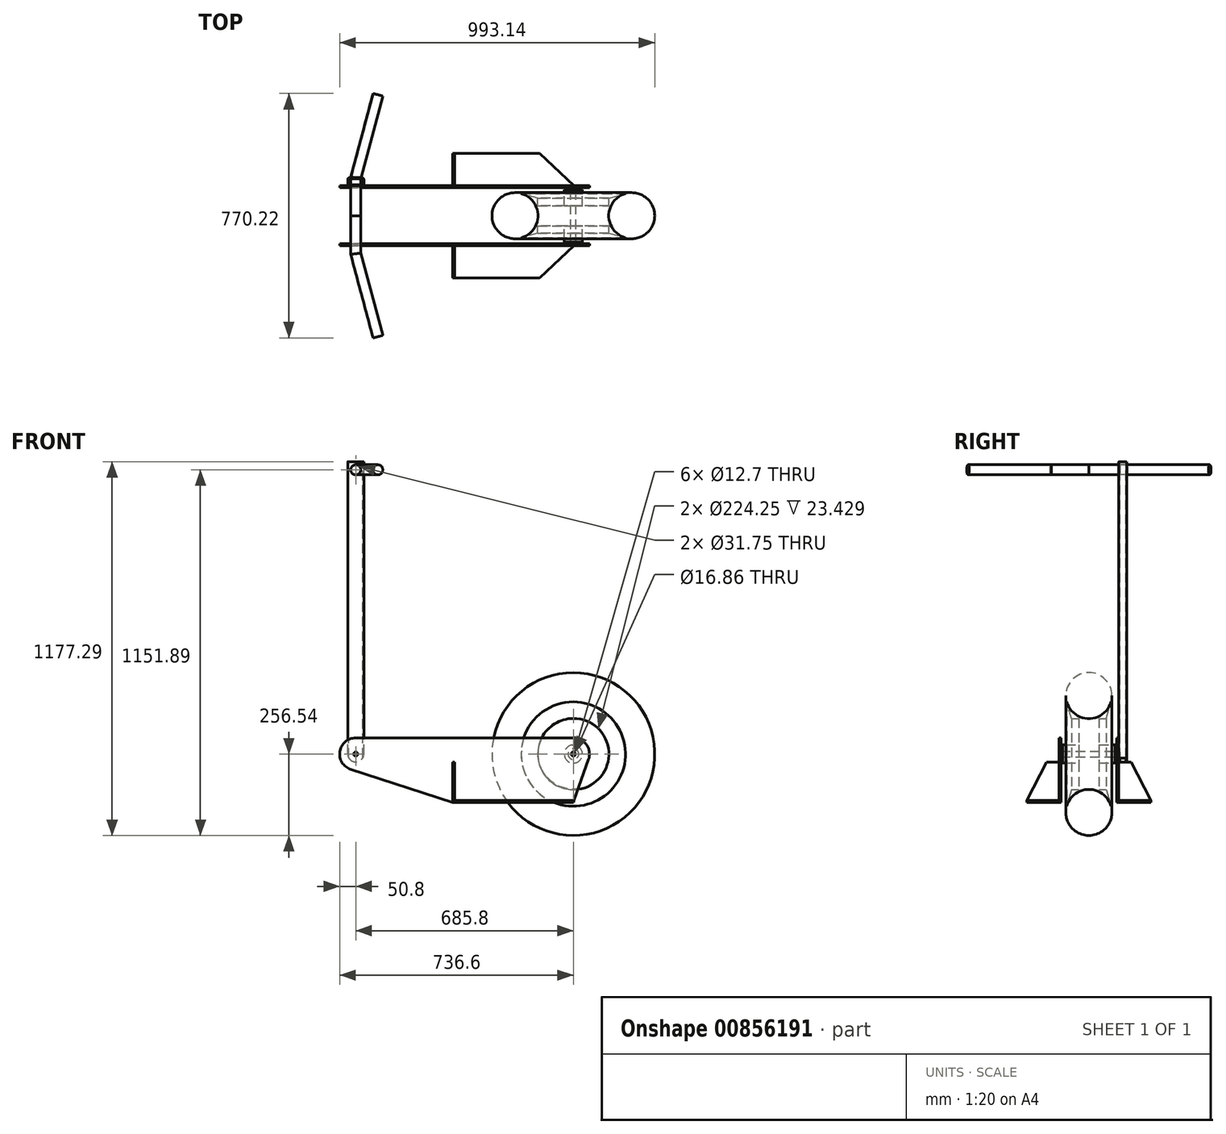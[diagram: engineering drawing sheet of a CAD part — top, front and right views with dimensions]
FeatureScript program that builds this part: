
annotation { "Feature Type Name" : "Feature", "Feature Type Description" : "" }
export const myFeature = defineFeature(function(context is Context, id is Id, definition is map)
    precondition{}
    {
        {
            var Q0;
            Q0=qCreatedBy(makeId("Front.planeOp"),FACE);
            var sketch = newSketch(context, id + "F0", { "sketchPlane" : qUnion([Q0])});
            skCircle(sketch, "E0", {"center": v(0, 0) * mm, "radius": 256.54 * mm});
            skPoint(sketch, "E0.first.point", {"position": v(0, 256.54) * mm});
            skPoint(sketch, "E0.second.point", {"position": v(248.73, -62.84) * mm});
            skPoint(sketch, "E0.third.point", {"position": v(-198.26, -162.81) * mm});
            skCircle(sketch, "E1", {"center": v(0, 0) * mm, "radius": 152.4 * mm});
            skPoint(sketch, "E1.first.point", {"position": v(0, 152.4) * mm});
            skPoint(sketch, "E1.second.point", {"position": v(151.83, -13.14) * mm});
            skPoint(sketch, "E1.third.point", {"position": v(-136.4, -68) * mm});
            skSolve(sketch);
        }
        {
            var Q0;
            Q0=qCreatedBy(makeId("Right.planeOp"),FACE);
            var sketch = newSketch(context, id + "F1", { "sketchPlane" : qUnion([Q0])});
            skPoint(sketch, "E2.0", {"position": v(0, 256.54) * mm});
            skLineSegment(sketch, "E2.1", {"start": v(0, -256.54) * mm, "end": v(0, 256.54) * mm, "construction": true});
            skLineSegment(sketch, "E3.bottom", {"start": v(82.52, 28.57) * mm, "end": v(-82.52, 28.58) * mm});
            skLineSegment(sketch, "E3.top", {"start": v(82.52, -28.57) * mm, "end": v(-82.52, -28.57) * mm});
            skLineSegment(sketch, "E3.left", {"start": v(82.52, 28.57) * mm, "end": v(82.52, 8.43) * mm});
            skLineSegment(sketch, "E3.right", {"start": v(-82.52, 28.58) * mm, "end": v(-82.52, 8.43) * mm});
            skPoint(sketch, "E3.middle", {"position": v(0, 0) * mm});
            skArc(sketch, "E4", {"start": v(71.4, 196.84) * mm, "mid": v(0, 256.54) * mm, "end": v(-71.4, 196.84) * mm});
            skLineSegment(sketch, "E5", {"start": v(71.4, 196.84) * mm, "end": v(-71.4, 196.84) * mm, "construction": true});
            skCircle(sketch, "E6", {"center": v(0, 184) * mm, "radius": 72.54 * mm});
            skLineSegment(sketch, "E7", {"start": v(69.84, 164.42) * mm, "end": v(55.18, 112.13) * mm});
            skLineSegment(sketch, "E8.MirrorCS", {"start": v(-69.84, 164.42) * mm, "end": v(-55.18, 112.13) * mm});
            skLineSegment(sketch, "E9", {"start": v(87.95, 8.43) * mm, "end": v(87.95, 16.86) * mm});
            skPoint(sketch, "E9.startSnap0", {"position": v(82.52, 0) * mm});
            skLineSegment(sketch, "E10", {"start": v(87.95, 16.86) * mm, "end": v(82.52, 16.86) * mm});
            skLineSegment(sketch, "E11", {"start": v(87.95, 0) * mm, "end": v(-87.95, 0) * mm});
            skLineSegment(sketch, "E12.MirrorCS", {"start": v(-87.95, 16.86) * mm, "end": v(-82.52, 16.86) * mm});
            skLineSegment(sketch, "E13.MirrorCS", {"start": v(-87.95, 8.43) * mm, "end": v(-87.95, 16.86) * mm});
            skLineSegment(sketch, "E14", {"start": v(31.75, 28.58) * mm, "end": v(31.75, 112.13) * mm});
            skLineSegment(sketch, "E15", {"start": v(31.75, 112.13) * mm, "end": v(55.18, 112.13) * mm});
            skLineSegment(sketch, "E16", {"start": v(55.18, 112.13) * mm, "end": v(31.75, 112.13) * mm});
            skLineSegment(sketch, "E17", {"start": v(-31.75, 28.58) * mm, "end": v(-31.75, 112.13) * mm});
            skLineSegment(sketch, "E18.trimOffspring", {"start": v(-31.75, 112.13) * mm, "end": v(-55.18, 112.13) * mm});
            skLineSegment(sketch, "E19", {"start": v(-87.95, 8.43) * mm, "end": v(87.95, 8.43) * mm});
            skLineSegment(sketch, "E20.trimOffspring", {"start": v(-82.52, 0) * mm, "end": v(-82.52, -28.57) * mm});
            skLineSegment(sketch, "E21.trimOffspring", {"start": v(82.52, 0) * mm, "end": v(82.52, -28.58) * mm});
            skSolve(sketch);
        }
        {
            var Q0;
            {var subQ0=sQuery(id+"F1.wireOp",EDGE,"E7");Q0=makeQuery(id+"F1.imprint","IMPRINT",FACE,{"disambiguationData":[TD([[makeQuery(id+"F1.imprint","IMPRINT",EDGE,{"derivedFrom":subQ0}),-1.0]])]});}
            var Q1;
            {var subQ0=sQuery(id+"F1.wireOp",EDGE,"E3.left");var subQ1=sQuery(id+"F1.wireOp",EDGE,"E3.bottom");var subQ2=makeQuery(id+"F1.imprint","INTERSECT",VERTEX,{"derivedFrom":[subQ1,subQ0]});Q1=makeQuery(id+"F1.imprint","IMPRINT",FACE,{"disambiguationData":[TD([[makeQuery(id+"F1.imprint","IMPRINT",EDGE,{"disambiguationData":[TD([[subQ2,-1.0]])],"derivedFrom":subQ1}),1.0]])]});}
            var Q2;
            {var subQ4=sQuery(id+"F1.wireOp",EDGE,"E9");Q2=makeQuery(id+"F1.imprint","IMPRINT",FACE,{"disambiguationData":[TD([[makeQuery(id+"F1.imprint","IMPRINT",EDGE,{"derivedFrom":subQ4}),1.0]])]});}
            var Q3;
            {var subQ0=sQuery(id+"F1.wireOp",EDGE,"E12.MirrorCS");Q3=makeQuery(id+"F1.imprint","IMPRINT",FACE,{"disambiguationData":[TD([[makeQuery(id+"F1.imprint","IMPRINT",EDGE,{"derivedFrom":subQ0}),-1.0]])]});}
            var Q4;
            Q4=sQuery(id+"F1.wireOp",EDGE,"E11");
            revolve(context, id + "F2", {"surfaceOperationType" : NewSurfaceOperationType.NEW, "entities" : qUnion([Q0, Q1, Q2, Q3]), "axis" : qUnion([Q4]), "revolveType" : RevolveType.FULL});
        }
        {
            var Q0;
            {var subQ0=sQuery(id+"F1.wireOp",EDGE,"E6");var subQ1=makeQuery(id+"F1.imprint","INTERSECT",VERTEX,{"derivedFrom":[subQ0,sQuery(id+"F1.wireOp",EDGE,"E7")]});Q0=makeQuery(id+"F1.imprint","IMPRINT",FACE,{"disambiguationData":[TD([[makeQuery(id+"F1.imprint","IMPRINT",EDGE,{"disambiguationData":[TD([[subQ1,-1.0]])],"derivedFrom":subQ0}),1.0]])]});}
            var Q1;
            Q1=sQuery(id+"F1.wireOp",EDGE,"E11");
            revolve(context, id + "F3", {"surfaceOperationType" : NewSurfaceOperationType.NEW, "entities" : qUnion([Q0]), "axis" : qUnion([Q1]), "revolveType" : RevolveType.FULL});
        }
        {
            var Q0;
            Q0=makeQuery(id+"F2.opRevolve","SWEPT_FACE",FACE,{"disambiguationData":[OSD([sQuery(id+"F1.wireOp",EDGE,"E9")])]});
            var sketch = newSketch(context, id + "F4", { "sketchPlane" : qUnion([Q0])});
            skLineSegment(sketch, "E22", {"start": v(0, 0) * mm, "end": v(685.8, 0) * mm, "construction": true});
            skCircle(sketch, "E23", {"center": v(685.8, 0) * mm, "radius": 256.54 * mm, "construction": true});
            skLineSegment(sketch, "E24", {"start": v(0, -152.4) * mm, "end": v(381, -152.4) * mm, "construction": true});
            skCircle(sketch, "E25.0", {"center": v(0, 0) * mm, "radius": 256.54 * mm, "construction": true});
            skLineSegment(sketch, "E26", {"start": v(-256.54, 0) * mm, "end": v(942.34, 0) * mm, "construction": true});
            skPoint(sketch, "E26.endSnap0", {"position": v(342.9, 0) * mm});
            skLineSegment(sketch, "E27", {"start": v(0, 0) * mm, "end": v(0, -63.15) * mm, "construction": true});
            skPoint(sketch, "E28.visualSharp", {"position": v(-50.8, 25.4) * mm});
            skCircle(sketch, "E29", {"center": v(0, 0) * mm, "radius": 6.35 * mm});
            skCircle(sketch, "E30", {"center": v(685.8, 0) * mm, "radius": 6.35 * mm});
            skLineSegment(sketch, "E31", {"start": v(-105.93, -256.54) * mm, "end": v(75.98, -256.54) * mm, "construction": true});
            skCircle(sketch, "E32", {"center": v(0, 0) * mm, "radius": 152.4 * mm});
            skPoint(sketch, "E33.orphan", {"position": v(-38.1, -152.4) * mm});
            skLineSegment(sketch, "E34", {"start": v(-152.4, 0) * mm, "end": v(-146.05, 0) * mm});
            skArc(sketch, "E35", {"start": v(0, 50.8) * mm, "mid": v(-41.48, 29.33) * mm, "end": v(-47.9, -16.93) * mm});
            skArc(sketch, "E36", {"start": v(701.5, -48.32) * mm, "mid": v(735.98, 7.94) * mm, "end": v(685.8, 50.8) * mm});
            skLineSegment(sketch, "E37", {"start": v(-55.72, 5.2) * mm, "end": v(0, -152.4) * mm});
            skLineSegment(sketch, "E38", {"start": v(0, -152.4) * mm, "end": v(381, -152.4) * mm});
            skLineSegment(sketch, "E39", {"start": v(381, -152.4) * mm, "end": v(701.5, -48.32) * mm});
            skLineSegment(sketch, "E40", {"start": v(0, 50.8) * mm, "end": v(685.8, 50.8) * mm});
            skLineSegment(sketch, "E41", {"start": v(-2.25, -146.05) * mm, "end": v(374.65, -146.05) * mm});
            skLineSegment(sketch, "E42", {"start": v(374.65, -146.05) * mm, "end": v(374.65, 50.8) * mm});
            skLineSegment(sketch, "E43", {"start": v(381, -152.4) * mm, "end": v(381, 50.8) * mm});
            skLineSegment(sketch, "E44", {"start": v(374.65, -146.05) * mm, "end": v(381, -146.05) * mm});
            skLineSegment(sketch, "E45", {"start": v(374.65, -25.4) * mm, "end": v(381, -25.4) * mm});
            skSolve(sketch);
        }
        {
            var Q0;
            Q0=makeQuery(id+"F4.imprint","IMPRINT",FACE,{"disambiguationData":[TD([[makeQuery(id+"F4.imprint","IMPRINT",EDGE,{"derivedFrom":sQuery(id+"F4.wireOp",EDGE,"E29")}),-1.0]])]});
            var Q1;
            {var subQ0=sQuery(id+"F1.wireOp",EDGE,"E9");Q1=makeQuery(id+"F4.imprint","IMPRINT",FACE,{"disambiguationData":[TD([[makeQuery(id+"F4.imprint","IMPRINT",EDGE,{"derivedFrom":makeQuery(id+"F2.opRevolve","SWEPT_EDGE",EDGE,{"disambiguationData":[OSD([subQ0,sQuery(id+"F1.wireOp",EDGE,"E19")])]})}),-1.0]])]});}
            var Q2;
            Q2=makeQuery(id+"F4.imprint","IMPRINT",FACE,{"disambiguationData":[TD([[makeQuery(id+"F4.imprint","IMPRINT",EDGE,{"derivedFrom":sQuery(id+"F4.wireOp",EDGE,"E30")}),-1.0]])]});
            var Q3;
            {var subQ0=sQuery(id+"F4.wireOp",EDGE,"E37");var subQ3=sQuery(id+"F4.wireOp",EDGE,"E41");var subQ5=makeQuery(id+"F4.imprint","INTERSECT",VERTEX,{"derivedFrom":[subQ0,subQ3]});Q3=makeQuery(id+"F4.imprint","IMPRINT",FACE,{"disambiguationData":[TD([[makeQuery(id+"F4.imprint","IMPRINT",EDGE,{"disambiguationData":[TD([[subQ5,-1.0]])],"derivedFrom":subQ3}),-1.0]])]});}
            var Q4;
            {var subQ5=sQuery(id+"F4.wireOp",EDGE,"E42");Q4=makeQuery(id+"F4.imprint","IMPRINT",FACE,{"disambiguationData":[TD([[makeQuery(id+"F4.imprint","IMPRINT",EDGE,{"derivedFrom":subQ5}),1.0]])]});}
            var Q5;
            {var subQ0=sQuery(id+"F4.wireOp",EDGE,"E42");Q5=makeQuery(id+"F4.imprint","IMPRINT",FACE,{"disambiguationData":[TD([[makeQuery(id+"F4.imprint","IMPRINT",EDGE,{"derivedFrom":subQ0}),-1.0]])]});}
            var Q6;
            {var subQ4=sQuery(id+"F4.wireOp",EDGE,"E38");Q6=makeQuery(id+"F4.imprint","IMPRINT",FACE,{"disambiguationData":[TD([[makeQuery(id+"F4.imprint","IMPRINT",EDGE,{"derivedFrom":subQ4}),1.0]])]});}
            var Q7;
            {var subQ1=sQuery(id+"F4.wireOp",EDGE,"E35");Q7=makeQuery(id+"F4.imprint","IMPRINT",FACE,{"disambiguationData":[TD([[makeQuery(id+"F4.imprint","IMPRINT",EDGE,{"derivedFrom":subQ1}),1.0]])]});}
            extrude(context, id + "F5", {"entities" : qUnion([Q0, Q1, Q2, Q3, Q4, Q5, Q6, Q7]), "depth" : 6.35 * mm, "offsetDistance" : 25.4 * mm});
        }
        {
            var Q0;
            Q0=makeQuery(id+"F5.opExtrude","CAP_FACE",FACE,{"disambiguationData":[OSD([sQuery(id+"F4.wireOp",EDGE,"E29"),sQuery(id+"F4.wireOp",EDGE,"E30"),sQuery(id+"F4.wireOp",EDGE,"E35"),sQuery(id+"F4.wireOp",EDGE,"E36"),sQuery(id+"F4.wireOp",EDGE,"E37"),sQuery(id+"F4.wireOp",EDGE,"E38"),sQuery(id+"F4.wireOp",EDGE,"E39"),sQuery(id+"F4.wireOp",EDGE,"E40")])],"isStart":false});
            var sketch = newSketch(context, id + "F6", { "sketchPlane" : qUnion([Q0])});
            skLineSegment(sketch, "E46.0", {"start": v(374.65, -146.05) * mm, "end": v(374.65, 50.8) * mm});
            skLineSegment(sketch, "E46.1", {"start": v(381, -152.4) * mm, "end": v(381, 50.8) * mm});
            skLineSegment(sketch, "E46.2", {"start": v(-2.25, -146.05) * mm, "end": v(374.65, -146.05) * mm});
            skLineSegment(sketch, "E46.3", {"start": v(0, -152.4) * mm, "end": v(381, -152.4) * mm});
            skLineSegment(sketch, "E46.4", {"start": v(-55.72, 5.2) * mm, "end": v(0, -152.4) * mm});
            skLineSegment(sketch, "E46.5", {"start": v(0, 50.8) * mm, "end": v(685.8, 50.8) * mm});
            skLineSegment(sketch, "E47.0", {"start": v(374.65, -146.05) * mm, "end": v(381, -146.05) * mm});
            skLineSegment(sketch, "E48.0", {"start": v(374.65, -25.4) * mm, "end": v(381, -25.4) * mm});
            skSolve(sketch);
        }
        {
            var Q0;
            Q0 = qSketchRegion(id + "F6", true);
            extrude(context, id + "F7", {"entities" : qUnion([Q0]), "operationType" : NewBodyOperationType.ADD, "depth" : 101.6 * mm, "offsetDistance" : 25.4 * mm});
        }
        {
            var Q0;
            Q0=makeQuery(id+"F7.opExtrude","SWEPT_FACE",FACE,{"disambiguationData":[OSD([sQuery(id+"F6.wireOp",EDGE,"E46.0")])]});
            var sketch = newSketch(context, id + "F8", { "sketchPlane" : qUnion([Q0])});
            skLineSegment(sketch, "E49", {"start": v(94.3, 50.8) * mm, "end": v(195.9, -146.05) * mm});
            skPoint(sketch, "E50.0", {"position": v(87.95, -25.4) * mm});
            skLineSegment(sketch, "E51", {"start": v(87.95, -25.4) * mm, "end": v(133.63, -25.4) * mm});
            skSolve(sketch);
        }
        {
            var Q0;
            Q0 = qSketchRegion(id + "F8", true);
            var Q1;
            Q1=makeQuery(id+"F8.imprint","IMPRINT",FACE,{"disambiguationData":[TD([[makeQuery(id+"F8.imprint","IMPRINT",EDGE,{"derivedFrom":sQuery(id+"F8.wireOp",EDGE,"E49")}),1.0]])]});
            var Q2;
            {var subQ0=sQuery(id+"F8.wireOp",EDGE,"E49");var subQ4=sQuery(id+"F8.wireOp",EDGE,"E51");var subQ5=makeQuery(id+"F8.imprint","INTERSECT",VERTEX,{"derivedFrom":[subQ0,subQ4]});Q2=makeQuery(id+"F8.imprint","IMPRINT",FACE,{"disambiguationData":[TD([[makeQuery(id+"F8.imprint","IMPRINT",EDGE,{"disambiguationData":[TD([[subQ5,1.0]])],"derivedFrom":subQ4}),1.0]])]});}
            extrude(context, id + "F9", {"entities" : qUnion([Q0, Q1, Q2]), "operationType" : NewBodyOperationType.REMOVE, "oppositeDirection" : true, "depth" : 25.4 * mm, "offsetDistance" : 25.4 * mm});
        }
        {
            var Q0;
            Q0=makeQuery(id+"F7.opExtrude","CAP_EDGE",EDGE,{"disambiguationData":[OSD([sQuery(id+"F6.wireOp",EDGE,"E46.4")])],"isStart":false});
            chamfer(context, id + "F10", {"entities" : qUnion([Q0]), "width" : 101.6 * mm, "tangentPropagation" : true});
        }
        {
            var Q0;
            Q0=makeQuery(id+"F5.opExtrude","SWEPT_BODY",BODY,{"disambiguationData":[OSD([sQuery(id+"F4.wireOp",EDGE,"E29"),sQuery(id+"F4.wireOp",EDGE,"E30"),sQuery(id+"F4.wireOp",EDGE,"E35"),sQuery(id+"F4.wireOp",EDGE,"E36"),sQuery(id+"F4.wireOp",EDGE,"E37"),sQuery(id+"F4.wireOp",EDGE,"E38"),sQuery(id+"F4.wireOp",EDGE,"E39"),sQuery(id+"F4.wireOp",EDGE,"E40")])]});
            var Q1;
            Q1=qCreatedBy(makeId("Front.planeOp"),FACE);
            mirror(context, id + "F11", {"entities" : qUnion([Q0]), "mirrorPlane" : qUnion([Q1])});
        }
        {
            var Q0;
            {var subQ0=sQuery(id+"F6.wireOp",EDGE,"E46.0");var subQ1=makeQuery(id+"F7.opExtrude","CAP_EDGE",EDGE,{"disambiguationData":[OSD([subQ0])],"isStart":true});var subQ3=sQuery(id+"F4.wireOp",EDGE,"E38");var subQ4=sQuery(id+"F4.wireOp",EDGE,"E36");var subQ5=sQuery(id+"F4.wireOp",EDGE,"E39");var subQ7=sQuery(id+"F4.wireOp",EDGE,"E30");var subQ8=sQuery(id+"F4.wireOp",EDGE,"E40");var subQ10=sQuery(id+"F4.wireOp",EDGE,"E37");var subQ11=sQuery(id+"F4.wireOp",EDGE,"E35");var subQ12=sQuery(id+"F4.wireOp",EDGE,"E29");var subQ13=makeQuery(id+"F5.opExtrude","CAP_FACE",FACE,{"disambiguationData":[OSD([subQ12,subQ7,subQ11,subQ4,subQ10,subQ3,subQ5,subQ8])],"isStart":false});Q0=makeQuery(id+"F9.boolean.opBoolean","MERGE",FACE,{"derivedFrom":[makeQuery(id+"F7.boolean.opBoolean","SPLIT",FACE,{"disambiguationData":[TD([makeQuery(id+"F5.opExtrude","SWEPT_FACE",FACE,{"disambiguationData":[OSD([subQ12])]})])],"derivedFrom":subQ13}),makeQuery(id+"F7.boolean.opBoolean","SPLIT",FACE,{"disambiguationData":[TD([makeQuery(id+"F5.opExtrude","SWEPT_FACE",FACE,{"disambiguationData":[OSD([subQ7])]})])],"derivedFrom":subQ13}),makeQuery(id+"F9.opExtrude","SWEPT_FACE",FACE,{"disambiguationData":[OSD([subQ0]),TDD([makeQuery(id+"F8.imprint","IMPRINT",EDGE,{"disambiguationData":[TD([[makeQuery(id+"F8.imprint","INTERSECT",VERTEX,{"derivedFrom":[subQ1,sQuery(id+"F8.wireOp",EDGE,"E51")]}),-1.0]])],"derivedFrom":subQ1})])]})]});}
            var sketch = newSketch(context, id + "F12", { "sketchPlane" : qUnion([Q0])});
            skLineSegment(sketch, "E52", {"start": v(660.4, 0) * mm, "end": v(660.4, 920.75) * mm});
            skArc(sketch, "E53", {"start": v(660.4, 0) * mm, "mid": v(685.8, -25.4) * mm, "end": v(711.2, 0) * mm});
            skLineSegment(sketch, "E54", {"start": v(711.2, 0) * mm, "end": v(711.2, 920.75) * mm});
            skLineSegment(sketch, "E55", {"start": v(660.4, 920.75) * mm, "end": v(711.2, 920.75) * mm});
            skCircle(sketch, "E56", {"center": v(685.8, 895.35) * mm, "radius": 15.88 * mm});
            skPoint(sketch, "E56.centerSnap0", {"position": v(685.8, 920.75) * mm});
            skSolve(sketch);
        }
        {
            var Q0;
            {var subQ0=sQuery(id+"F12.wireOp",EDGE,"E55");Q0=makeQuery(id+"F12.imprint","IMPRINT",FACE,{"disambiguationData":[TD([[makeQuery(id+"F12.imprint","IMPRINT",EDGE,{"derivedFrom":subQ0}),-1.0]])]});}
            var Q1;
            {var subQ1=sQuery(id+"F12.wireOp",EDGE,"E53");Q1=makeQuery(id+"F12.imprint","IMPRINT",FACE,{"disambiguationData":[TD([[makeQuery(id+"F12.imprint","IMPRINT",EDGE,{"derivedFrom":subQ1}),1.0]])]});}
            extrude(context, id + "F13", {"entities" : qUnion([Q0, Q1]), "depth" : 25.4 * mm, "offsetDistance" : 25.4 * mm});
        }
        {
            var Q0;
            Q0=makeQuery(id+"F13.opExtrude","CAP_EDGE",EDGE,{"disambiguationData":[OSD([sQuery(id+"F12.wireOp",EDGE,"E52")])],"isStart":false});
            var Q1;
            Q1=makeQuery(id+"F13.opExtrude","CAP_EDGE",EDGE,{"disambiguationData":[OSD([sQuery(id+"F12.wireOp",EDGE,"E54")])],"isStart":false});
            var Q2;
            Q2=makeQuery(id+"F13.opExtrude","CAP_EDGE",EDGE,{"disambiguationData":[OSD([sQuery(id+"F12.wireOp",EDGE,"E52")])],"isStart":true});
            fillet(context, id + "F14", {"entities" : qUnion([Q0, Q1, Q2]), "radius" : 5.08 * mm, "tangentPropagation" : true, "allowEdgeOverflow" : false});
        }
        {
            var Q0;
            Q0=makeQuery(id+"F13.opExtrude","SWEPT_FACE",FACE,{"disambiguationData":[OSD([sQuery(id+"F12.wireOp",EDGE,"E55")])]});
            var sketch = newSketch(context, id + "F15", { "sketchPlane" : qUnion([Q0])});
            skLineSegment(sketch, "E57.0", {"start": v(-663.58, 116.52) * mm, "end": v(-663.58, 97.47) * mm});
            skLineSegment(sketch, "E57.1", {"start": v(-663.58, 116.52) * mm, "end": v(-708.02, 116.52) * mm});
            skLineSegment(sketch, "E57.2", {"start": v(-708.02, 116.52) * mm, "end": v(-708.02, 97.47) * mm});
            skLineSegment(sketch, "E57.3", {"start": v(-663.58, 97.47) * mm, "end": v(-708.02, 97.47) * mm});
            skSolve(sketch);
        }
        {
            var Q0;
            Q0=makeQuery(id+"F15.imprint","IMPRINT",FACE,{"disambiguationData":[TD([[makeQuery(id+"F15.imprint","IMPRINT",EDGE,{"derivedFrom":sQuery(id+"F15.wireOp",EDGE,"E57.0")}),-1.0]])]});
            extrude(context, id + "F16", {"entities" : qUnion([Q0]), "operationType" : NewBodyOperationType.REMOVE, "endBound" : BoundingType.THROUGH_ALL, "oppositeDirection" : true, "depth" : 25.4 * mm, "offsetDistance" : 25.4 * mm});
        }
        {
            var Q0;
            Q0=qCreatedBy(makeId("Front.planeOp"),FACE);
            var sketch = newSketch(context, id + "F17", { "sketchPlane" : qUnion([Q0])});
            skCircle(sketch, "E58.0", {"center": v(-685.8, 895.35) * mm, "radius": 15.88 * mm});
            skSolve(sketch);
        }
        {
            var Q0;
            Q0=makeQuery(id+"F13.opExtrude","CAP_FACE",FACE,{"disambiguationData":[OSD([sQuery(id+"F4.wireOp",EDGE,"E30"),sQuery(id+"F12.wireOp",EDGE,"E52"),sQuery(id+"F12.wireOp",EDGE,"E53"),sQuery(id+"F12.wireOp",EDGE,"E54"),sQuery(id+"F12.wireOp",EDGE,"E55"),sQuery(id+"F12.wireOp",EDGE,"E56")])],"isStart":false});
            var sketch = newSketch(context, id + "F18", { "sketchPlane" : qUnion([Q0])});
            skSolve(sketch);
        }
        {
            var Q0;
            Q0=makeQuery(id+"F7.opExtrude","SWEPT_FACE",FACE,{"disambiguationData":[OSD([sQuery(id+"F6.wireOp",EDGE,"E46.2")])]});
            var Q1;
            Q1=sQuery(id+"F17.wireOp",VERTEX,"E58.0.center");
            cPlane(context, id + "F19", {"entities" : qUnion([Q0, Q1]), "cplaneType" : CPlaneType.PLANE_POINT, "offset" : 25.4 * mm, "width" : 152.4 * mm, "height" : 152.4 * mm});
        }
        {
            var Q0;
            Q0=qCreatedBy(id+"F19.planeOp",FACE);
            var sketch = newSketch(context, id + "F20", { "sketchPlane" : qUnion([Q0])});
            skPoint(sketch, "E59.0", {"position": v(-685.8, 0) * mm});
            skLineSegment(sketch, "E59.1", {"start": v(-701.67, 119.7) * mm, "end": v(-669.92, 119.7) * mm});
            skLineSegment(sketch, "E60", {"start": v(-685.8, 0) * mm, "end": v(-685.8, 119.7) * mm});
            skLineSegment(sketch, "E61", {"start": v(-685.8, 119.7) * mm, "end": v(-615.78, 381) * mm});
            skSolve(sketch);
        }
        {
            var Q0;
            Q0=qCreatedBy(makeId("Front.planeOp"),FACE);
            var Q1;
            Q1=sQuery(id+"F20.wireOp",VERTEX,"E61.end");
            cPlane(context, id + "F21", {"entities" : qUnion([Q0, Q1]), "cplaneType" : CPlaneType.PLANE_POINT, "offset" : 25.4 * mm, "width" : 152.4 * mm, "height" : 152.4 * mm});
        }
        {
            var Q0;
            Q0=qCreatedBy(id+"F21.planeOp",FACE);
            var sketch = newSketch(context, id + "F22", { "sketchPlane" : qUnion([Q0])});
            skPoint(sketch, "E62.0", {"position": v(-615.78, 895.35) * mm});
            skCircle(sketch, "E63", {"center": v(-615.78, 895.35) * mm, "radius": 15.88 * mm});
            skSolve(sketch);
        }
        {
            var Q0;
            Q0=makeQuery(id+"F22.imprint","IMPRINT",FACE,{"disambiguationData":[TD([[makeQuery(id+"F22.imprint","IMPRINT",EDGE,{"derivedFrom":sQuery(id+"F22.wireOp",EDGE,"E63")}),1.0]])]});
            var Q1;
            Q1=makeQuery(id+"F18.imprint","IMPRINT",FACE,{"disambiguationData":[TD([[makeQuery(id+"F18.imprint","IMPRINT",EDGE,{"derivedFrom":makeQuery(id+"F13.opExtrude","CAP_EDGE",EDGE,{"disambiguationData":[OSD([sQuery(id+"F12.wireOp",EDGE,"E56")])],"isStart":false})}),1.0]])]});
            var Q2;
            Q2=makeQuery(id+"F17.imprint","IMPRINT",FACE,{"disambiguationData":[TD([[makeQuery(id+"F17.imprint","IMPRINT",EDGE,{"derivedFrom":sQuery(id+"F17.wireOp",EDGE,"E58.0")}),1.0]])]});
            var Q3;
            Q3=sQuery(id+"F20.wireOp",EDGE,"E61");
            var Q4;
            Q4=sQuery(id+"F20.wireOp",EDGE,"E60");
            sweep(context, id + "F23", {"profiles" : qUnion([Q0, Q1, Q2]), "path" : qUnion([Q3, Q4])});
        }
        {
            var Q0;
            Q0=makeQuery(id+"F23.opSweep","SWEPT_BODY",BODY,{"disambiguationData":[OSD([sQuery(id+"F17.wireOp",EDGE,"E58.0"),sQuery(id+"F20.wireOp",EDGE,"E60")])]});
            var Q1;
            Q1=makeQuery(id+"F23.opSweep","CAP_FACE",FACE,{"disambiguationData":[OSD([sQuery(id+"F17.wireOp",EDGE,"E58.0"),sQuery(id+"F20.wireOp",VERTEX,"E60.start")])],"isStart":true});
            mirror(context, id + "F24", {"entities" : qUnion([Q0]), "mirrorPlane" : qUnion([Q1])});
        }
        {
            var Q0;
            Q0=makeQuery(id+"F23.opSweep","SWEPT_BODY",BODY,{"disambiguationData":[OSD([sQuery(id+"F20.wireOp",EDGE,"E60"),sQuery(id+"F22.wireOp",EDGE,"E63")])]});
            deleteBodies(context, id + "F25", {"entities" : qUnion([Q0])});
        }
    });
